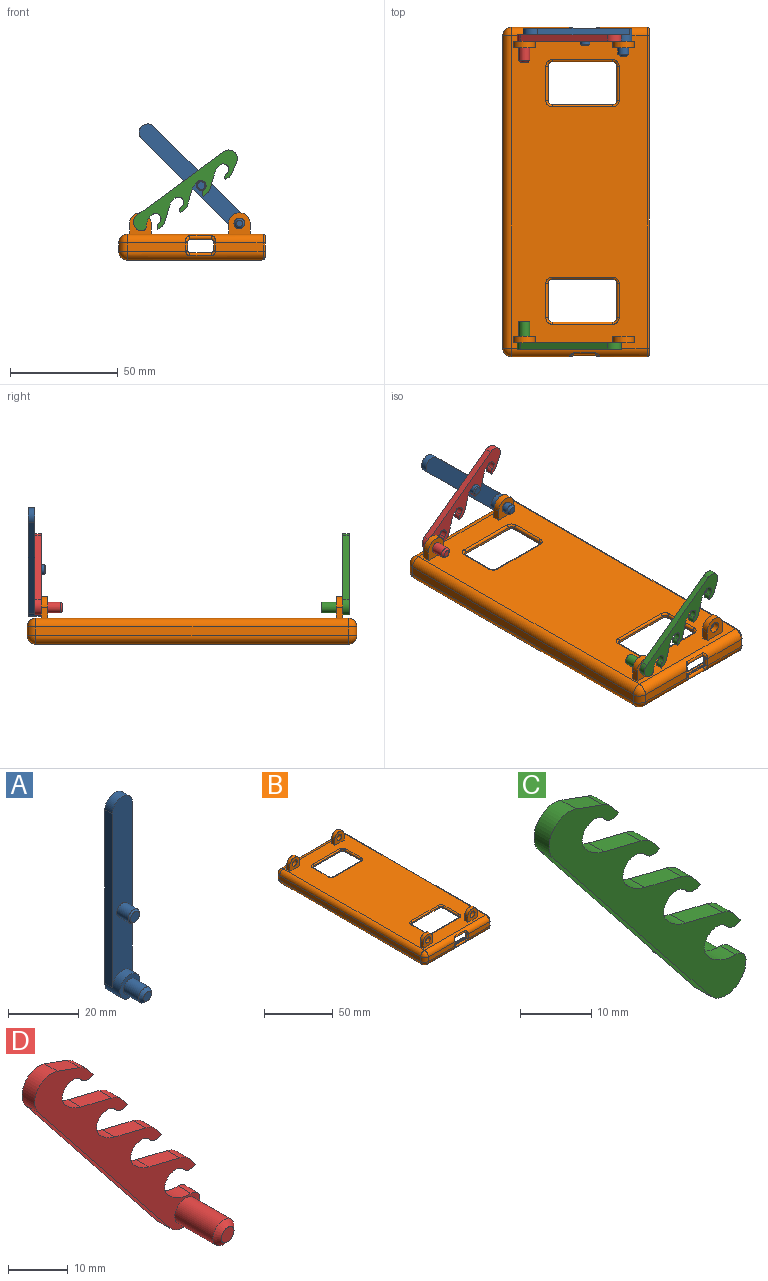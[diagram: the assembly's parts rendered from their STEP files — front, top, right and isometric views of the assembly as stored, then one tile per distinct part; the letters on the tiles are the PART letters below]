
ASSEMBLY  parts=4 mates=7
PART A: 13 faces, bbox 8x13x68 mm
  f0: plane 60x3mm, normal (-1,0,0), area 180mm2, adj f1,f3,f4,f5
  f1: cylinder r=4mm len=8mm, axis (0,1,0), area 113.1mm2, adj f0,f2,f4,f5,f6
  f2: plane 60x3mm, normal (1,0,0), area 180mm2, adj f1,f3,f4,f5
  f3: cylinder r=4mm len=8mm, axis (0,1,0), area 37.7mm2, adj f0,f2,f4,f5
  f4: plane 64x8mm, normal (0,-1,0), area 464.1mm2, adj f0,f1,f2,f3,f9
  f5: plane 68x8mm, normal (0,1,0), area 530.3mm2, adj f0,f1,f2,f3
  f6: plane 8x8mm, normal (0,-1,0), area 30.6mm2, adj f1,f8
  f7: plane 3x3mm, normal (0,-1,0), area 7.1mm2, adj f11
  f8: cylinder r=2.5mm len=6mm, axis (0,1,0), area 94.2mm2, adj f6,f11
  f9: cylinder r=2.25mm len=4.5mm, axis (0,1,0), area 63.6mm2, adj f4,f12
  f10: plane 3.5x3.5mm, normal (0,-1,0), area 9.6mm2, adj f12
  f11: cone r=1.5mm half-angle=45deg, axis (0,1,0), area 17.8mm2, adj f7,f8
  f12: cone r=1.75mm half-angle=45deg, axis (0,1,0), area 8.9mm2, adj f9,f10
PART B: 152 faces, bbox 68.1x155x22 mm
  f0: plane 145x63mm, normal (0,0,1), area 7534.5mm2, adj f9,f10,f14,f86,f104,f105,f106,f107
  f1: plane 145x63mm, normal (0,0,-1), area 7861.9mm2, adj f23,f24,f30,f66,f67,f68,f69,f70
  f2: plane 145x62.24mm, normal (0,0,-1), area 281.5mm2, adj f11,f12,f21,f95,f96,f97,f98,f99
  f3: plane 27.06x4mm, normal (0,1,0), area 108mm2, adj f9,f12,f17,f74,f75
  f4: plane 27.06x4mm, normal (0,-1,0), area 108mm2, adj f10,f11,f18,f60,f62
  f5: plane 22.06x4mm, normal (0,-1,0), area 88mm2, adj f10,f11,f59,f61,f90
  f6: plane 28.13x4mm, normal (0,-1,0), area 112mm2, adj f23,f28,f33,f42,f44
  f7: plane 28.13x4mm, normal (0,1,0), area 112mm2, adj f24,f26,f34,f49,f52
  f8: plane 22.06x4mm, normal (0,1,0), area 88mm2, adj f9,f12,f83,f85,f89
  f9: cylinder r=4mm len=63mm, axis (1,0,0), area 344mm2, adj f0,f3,f8,f15,f76,f78,f80,f82
  f10: cylinder r=4mm len=63mm, axis (1,0,0), area 344mm2, adj f0,f4,f5,f16,f54,f55,f56,f57
  f11: cylinder r=4mm len=63mm, axis (1,0,0), area 368.3mm2, adj f2,f4,f5,f20,f63,f64,f65,f92
  f12: cylinder r=4mm len=63mm, axis (1,0,0), area 368.3mm2, adj f2,f3,f8,f19,f77,f79,f81,f91
  f13: plane 145x4mm, normal (-1,0,0), area 580mm2, adj f14,f17,f18,f21
  f14: cylinder r=4mm len=145mm, axis (0,1,0), area 911.1mm2, adj f0,f13,f15,f16
  f15: sphere r=4mm, area 25.1mm2, adj f9,f14,f17
  f16: sphere r=4mm, area 25.1mm2, adj f10,f14,f18
  f17: cylinder r=4mm len=4mm, axis (0,0,-1), area 25.1mm2, adj f3,f13,f15,f19
  f18: cylinder r=4mm len=4mm, axis (0,0,1), area 25.1mm2, adj f4,f13,f16,f20
  f19: sphere r=4mm, area 25.1mm2, adj f12,f17,f21
  f20: sphere r=4mm, area 25.1mm2, adj f11,f18,f21
  f21: cylinder r=4mm len=145mm, axis (0,-1,0), area 911.1mm2, adj f2,f13,f19,f20
  f22: plane 23.13x4mm, normal (0,-1,0), area 92mm2, adj f23,f28,f40,f43,f89
  f23: cylinder r=2mm len=63mm, axis (1,0,0), area 178.1mm2, adj f1,f6,f22,f31,f38,f39,f43,f44
  f24: cylinder r=2mm len=63mm, axis (1,0,0), area 178.1mm2, adj f1,f7,f25,f32,f46,f47,f48,f49
  f25: plane 23.13x4mm, normal (0,1,0), area 92mm2, adj f24,f26,f50,f53,f90
  f26: cylinder r=2mm len=63mm, axis (1,0,0), area 191.9mm2, adj f7,f25,f27,f36,f51,f52,f53,f92
  f27: plane 145x62.24mm, normal (0,0,1), area 281.5mm2, adj f26,f28,f37,f95,f96,f97,f98,f99
  f28: cylinder r=2mm len=63mm, axis (1,0,0), area 191.9mm2, adj f6,f22,f27,f35,f40,f41,f42,f91
  f29: plane 145x4mm, normal (1,0,0), area 580mm2, adj f30,f33,f34,f37
  f30: cylinder r=2mm len=145mm, axis (0,1,0), area 455.5mm2, adj f1,f29,f31,f32
  f31: sphere r=2mm, area 6.3mm2, adj f23,f30,f33
  f32: sphere r=2mm, area 6.3mm2, adj f24,f30,f34
  f33: cylinder r=2mm len=4mm, axis (0,0,-1), area 12.6mm2, adj f6,f29,f31,f35
  f34: cylinder r=2mm len=4mm, axis (0,0,1), area 12.6mm2, adj f7,f29,f32,f36
  f35: sphere r=2mm, area 6.3mm2, adj f28,f33,f37
  f36: sphere r=2mm, area 6.3mm2, adj f26,f34,f37
  f37: cylinder r=2mm len=145mm, axis (0,-1,0), area 455.5mm2, adj f27,f29,f35,f36
  f38: plane 10x0.34mm, normal (0,0,-1), area 3.4mm2, adj f23,f39,f45,f80
  f39: cylinder r=1mm len=1.64mm, axis (0,-1,0), area 1.1mm2, adj f23,f38,f43,f82
  f40: cylinder r=1mm len=1.06mm, axis (0,-1,0), area 1.3mm2, adj f22,f28,f41,f43,f81,f83
  f41: plane 10x0.66mm, normal (0,0,1), area 6.6mm2, adj f28,f40,f42,f79
  f42: cylinder r=1mm len=1.06mm, axis (0,-1,0), area 1.3mm2, adj f6,f28,f41,f44,f75,f77
  f43: plane 4x1.06mm, normal (-1,0,0), area 4mm2, adj f22,f23,f39,f40,f84,f85
  f44: plane 4x1.06mm, normal (1,0,0), area 4mm2, adj f6,f23,f42,f45,f74,f76
  f45: cylinder r=1mm len=1.64mm, axis (0,-1,0), area 1.1mm2, adj f23,f38,f44,f78
  f46: cylinder r=1mm len=1.64mm, axis (0,-1,0), area 1.1mm2, adj f24,f48,f49,f56
  f47: cylinder r=1mm len=1.64mm, axis (0,-1,0), area 1.1mm2, adj f24,f48,f50,f55
  f48: plane 10x0.34mm, normal (0,0,-1), area 3.4mm2, adj f24,f46,f47,f54
  f49: plane 4x1.06mm, normal (1,0,0), area 4mm2, adj f7,f24,f46,f52,f58,f60
  f50: plane 4x1.06mm, normal (-1,0,0), area 4mm2, adj f24,f25,f47,f53,f57,f59
  f51: plane 10x0.66mm, normal (0,0,1), area 6.6mm2, adj f26,f52,f53,f65
  f52: cylinder r=1mm len=1.06mm, axis (0,-1,0), area 1.3mm2, adj f7,f26,f49,f51,f62,f64
  f53: cylinder r=1mm len=1.06mm, axis (0,-1,0), area 1.3mm2, adj f25,f26,f50,f51,f61,f63
  f54: cylinder r=1mm len=10mm, axis (1,0,0), area 25.6mm2, adj f10,f48,f55,f56
  f55: bspline ~3.32x3.18mm, area 5.3mm2, adj f10,f47,f54,f57
  f56: bspline ~3.32x2.88mm, area 5.3mm2, adj f10,f46,f54,f58
  f57: torus R=3mm, axis (-1,0,0), area 1mm2, adj f10,f50,f55,f59
  f58: torus R=3mm, axis (-1,0,0), area 1mm2, adj f10,f49,f56,f60
  f59: cylinder r=1mm len=3.5mm, axis (0,0,1), area 5.5mm2, adj f5,f50,f57,f61
  f60: cylinder r=1mm len=3.5mm, axis (0,0,-1), area 5.5mm2, adj f4,f49,f58,f62
  f61: torus R=2mm, axis (0,1,0), area 0.5mm2, adj f5,f53,f59,f63
  f62: torus R=2mm, axis (0,1,0), area 0.5mm2, adj f4,f52,f60,f64
  f63: bspline ~2.57x2.42mm, area 3.6mm2, adj f11,f53,f61,f65
  f64: bspline ~2.57x2.42mm, area 3.6mm2, adj f11,f52,f62,f65
  f65: cylinder r=1mm len=10mm, axis (1,0,0), area 20.9mm2, adj f11,f51,f63,f64
  f66: plane 28x1mm, normal (0,1,0), area 28mm2, adj f1,f67,f73,f104
  f67: cylinder r=2mm len=2mm, axis (0,0,1), area 3.1mm2, adj f1,f66,f68,f105
  f68: plane 16x1mm, normal (-1,0,0), area 16mm2, adj f1,f67,f69,f107
  f69: cylinder r=2mm len=2mm, axis (0,0,1), area 3.1mm2, adj f1,f68,f70,f109
  f70: plane 28x1mm, normal (0,-1,0), area 28mm2, adj f1,f69,f71,f111
  f71: cylinder r=2mm len=2mm, axis (0,0,1), area 3.1mm2, adj f1,f70,f72,f110
  f72: plane 16x1mm, normal (1,0,0), area 16mm2, adj f1,f71,f73,f108
  f73: cylinder r=2mm len=2mm, axis (0,0,1), area 3.1mm2, adj f1,f66,f72,f106
  f74: cylinder r=1mm len=3.5mm, axis (0,0,-1), area 5.5mm2, adj f3,f44,f75,f76
  f75: torus R=2mm, axis (0,1,0), area 0.5mm2, adj f3,f42,f74,f77
  f76: torus R=3mm, axis (-1,0,0), area 1mm2, adj f9,f44,f74,f78
  f77: bspline ~2.57x2.42mm, area 3.6mm2, adj f12,f42,f75,f79
  f78: bspline ~3.32x3.18mm, area 5.3mm2, adj f9,f45,f76,f80
  f79: cylinder r=1mm len=10mm, axis (1,0,0), area 20.9mm2, adj f12,f41,f77,f81
  f80: cylinder r=1mm len=10mm, axis (1,0,0), area 25.6mm2, adj f9,f38,f78,f82
  f81: bspline ~2.57x2.42mm, area 3.6mm2, adj f12,f40,f79,f83
  f82: bspline ~3.32x3.18mm, area 5.3mm2, adj f9,f39,f80,f84
  f83: torus R=2mm, axis (0,1,0), area 0.5mm2, adj f8,f40,f81,f85
  f84: torus R=3mm, axis (-1,0,0), area 1mm2, adj f9,f43,f82,f85
  f85: cylinder r=1mm len=3.5mm, axis (0,0,1), area 5.5mm2, adj f8,f43,f83,f84
  f86: cylinder r=1mm len=145mm, axis (0,1,0), area 455.5mm2, adj f0,f1,f87,f88
  f87: torus R=3mm, axis (1,0,0), area 14.8mm2, adj f9,f23,f86,f89
  f88: torus R=3mm, axis (1,0,0), area 14.8mm2, adj f10,f24,f86,f90
  f89: cylinder r=1mm len=4mm, axis (0,0,-1), area 12.6mm2, adj f8,f22,f87,f91
  f90: cylinder r=1mm len=4mm, axis (0,0,1), area 12.6mm2, adj f5,f25,f88,f92
  f91: torus R=3mm, axis (1,0,0), area 7.9mm2, adj f12,f28,f89,f93,f102
  f92: torus R=3mm, axis (1,0,0), area 7.9mm2, adj f11,f26,f90,f94,f103
  f93: bspline ~3.73x2.32mm, area 3.6mm2, adj f28,f91,f95,f102
  f94: bspline ~3.73x2.32mm, area 3.6mm2, adj f26,f92,f96,f103
  f95: torus R=3mm, axis (0,0,1), area 9.6mm2, adj f2,f27,f93,f97,f102
  f96: torus R=3mm, axis (0,0,1), area 9.6mm2, adj f2,f27,f94,f98,f103
  f97: cylinder r=1mm len=53mm, axis (1,0,0), area 166.5mm2, adj f2,f27,f95,f99
  f98: cylinder r=1mm len=53mm, axis (-1,0,0), area 166.5mm2, adj f2,f27,f96,f100
  f99: torus R=6mm, axis (0,0,1), area 26.5mm2, adj f2,f27,f97,f101
  f100: torus R=6mm, axis (0,0,1), area 26.5mm2, adj f2,f27,f98,f101
  f101: cylinder r=1mm len=131mm, axis (0,1,0), area 411.5mm2, adj f2,f27,f99,f100
  f102: bspline ~4.62x2.29mm, area 5.4mm2, adj f12,f91,f93,f95
  f103: bspline ~4.62x2.29mm, area 5.4mm2, adj f11,f92,f94,f96
  f104: cylinder r=1mm len=28mm, axis (-1,0,0), area 44mm2, adj f0,f66,f105,f106
  f105: torus R=3mm, axis (0,0,1), area 5.8mm2, adj f0,f67,f104,f107
  f106: torus R=3mm, axis (0,0,1), area 5.8mm2, adj f0,f73,f104,f108
  f107: cylinder r=1mm len=16mm, axis (0,-1,0), area 25.1mm2, adj f0,f68,f105,f109
  f108: cylinder r=1mm len=16mm, axis (0,1,0), area 25.1mm2, adj f0,f72,f106,f110
  f109: torus R=3mm, axis (0,0,1), area 5.8mm2, adj f0,f69,f107,f111
  f110: torus R=3mm, axis (0,0,1), area 5.8mm2, adj f0,f71,f108,f111
  f111: cylinder r=1mm len=28mm, axis (1,0,0), area 44mm2, adj f0,f70,f109,f110
  f112: plane 28x1mm, normal (0,-1,0), area 28mm2, adj f1,f113,f119,f120
  f113: cylinder r=2mm len=2mm, axis (0,0,1), area 3.1mm2, adj f1,f112,f114,f122
  f114: plane 16x1mm, normal (1,0,0), area 16mm2, adj f1,f113,f115,f124
  f115: cylinder r=2mm len=2mm, axis (0,0,1), area 3.1mm2, adj f1,f114,f116,f126
  f116: plane 28x1mm, normal (0,1,0), area 28mm2, adj f1,f115,f117,f127
  f117: cylinder r=2mm len=2mm, axis (0,0,1), area 3.1mm2, adj f1,f116,f118,f125
  f118: plane 16x1mm, normal (-1,0,0), area 16mm2, adj f1,f117,f119,f123
  f119: cylinder r=2mm len=2mm, axis (0,0,1), area 3.1mm2, adj f1,f112,f118,f121
  f120: cylinder r=1mm len=28mm, axis (1,0,0), area 44mm2, adj f0,f112,f121,f122
  f121: torus R=3mm, axis (0,0,1), area 5.8mm2, adj f0,f119,f120,f123
  f122: torus R=3mm, axis (0,0,1), area 5.8mm2, adj f0,f113,f120,f124
  f123: cylinder r=1mm len=16mm, axis (0,-1,0), area 25.1mm2, adj f0,f118,f121,f125
  f124: cylinder r=1mm len=16mm, axis (0,1,0), area 25.1mm2, adj f0,f114,f122,f126
  f125: torus R=3mm, axis (0,0,1), area 5.8mm2, adj f0,f117,f123,f127
  f126: torus R=3mm, axis (0,0,1), area 5.8mm2, adj f0,f115,f124,f127
  f127: cylinder r=1mm len=28mm, axis (-1,0,0), area 44mm2, adj f0,f116,f125,f126
  f128: plane 5x3mm, normal (1,0,0), area 15mm2, adj f0,f129,f132,f133
  f129: cylinder r=5mm len=10mm, axis (0,1,0), area 47.1mm2, adj f128,f130,f132,f133
  f130: plane 5x3mm, normal (-1,0,0), area 15mm2, adj f0,f129,f132,f133
  f131: cylinder r=2.5mm len=5mm, axis (0,1,0), area 47.1mm2, adj f132,f133
  f132: plane 10x10mm, normal (0,-1,0), area 69.6mm2, adj f0,f128,f129,f130,f131
  f133: plane 10x10mm, normal (0,1,0), area 69.6mm2, adj f0,f128,f129,f130,f131
  f134: plane 5x3mm, normal (1,0,0), area 15mm2, adj f0,f137,f138,f139
  f135: plane 5x3mm, normal (-1,0,0), area 15mm2, adj f0,f137,f138,f139
  f136: cylinder r=2.5mm len=5mm, axis (0,-1,0), area 47.1mm2, adj f138,f139
  f137: cylinder r=5mm len=10mm, axis (0,-1,0), area 47.1mm2, adj f134,f135,f138,f139
  f138: plane 10x10mm, normal (0,1,0), area 69.6mm2, adj f0,f134,f135,f136,f137
  f139: plane 10x10mm, normal (0,-1,0), area 69.6mm2, adj f0,f134,f135,f136,f137
  f140: plane 5x3mm, normal (-1,0,0), area 15mm2, adj f0,f143,f144,f145
  f141: plane 5x3mm, normal (1,0,0), area 15mm2, adj f0,f143,f144,f145
  f142: cylinder r=2.5mm len=5mm, axis (0,1,0), area 47.1mm2, adj f144,f145
  f143: cylinder r=5mm len=10mm, axis (0,1,0), area 47.1mm2, adj f140,f141,f144,f145
  f144: plane 10x10mm, normal (0,-1,0), area 69.6mm2, adj f0,f140,f141,f142,f143
  f145: plane 10x10mm, normal (0,1,0), area 69.6mm2, adj f0,f140,f141,f142,f143
  f146: plane 5x3mm, normal (-1,0,0), area 15mm2, adj f0,f147,f150,f151
  f147: cylinder r=5mm len=10mm, axis (0,-1,0), area 47.1mm2, adj f146,f148,f150,f151
  f148: plane 5x3mm, normal (1,0,0), area 15mm2, adj f0,f147,f150,f151
  f149: cylinder r=2.5mm len=5mm, axis (0,-1,0), area 47.1mm2, adj f150,f151
  f150: plane 10x10mm, normal (0,1,0), area 69.6mm2, adj f0,f146,f147,f148,f149
  f151: plane 10x10mm, normal (0,-1,0), area 69.6mm2, adj f0,f146,f147,f148,f149
PART C: 32 faces, bbox 39.1x13x47.2 mm
  f0: plane 7.33x3mm, normal (0.24,0,0.97), area 22.6mm2, adj f1,f27,f28,f29
  f1: cylinder r=7mm len=3.8mm, axis (0,1,0), area 13.8mm2, adj f0,f2,f28,f29
  f2: cylinder r=2.5mm len=4.46mm, axis (0,1,0), area 23.6mm2, adj f1,f3,f28,f29
  f3: cylinder r=2mm len=3mm, axis (0,1,0), area 9.4mm2, adj f2,f4,f28,f29
  f4: plane 3x1.57mm, normal (0.78,0,0.62), area 6mm2, adj f3,f5,f28,f29
  f5: cylinder r=4.5mm len=3mm, axis (0,1,0), area 7.5mm2, adj f4,f6,f28,f29
  f6: plane 5.24x3mm, normal (0.34,0,0.94), area 16.7mm2, adj f5,f7,f28,f29
  f7: cylinder r=4mm len=6.49mm, axis (0,1,0), area 31.1mm2, adj f6,f8,f28,f29
  f8: plane 39.16x31.09mm, normal (-0.78,0,-0.62), area 150mm2, adj f7,f9,f28,f29
  f9: cylinder r=4mm len=7.13mm, axis (0,1,0), area 30mm2, adj f8,f10,f28,f29
  f10: cylinder r=2mm len=3mm, axis (0,1,0), area 9.4mm2, adj f9,f11,f28,f29
  f11: cylinder r=7mm len=5.68mm, axis (0,1,0), area 19.5mm2, adj f10,f12,f28,f29
  f12: cylinder r=2.5mm len=4.46mm, axis (0,1,0), area 23.6mm2, adj f11,f13,f28,f29
  f13: cylinder r=2mm len=3mm, axis (0,1,0), area 9.4mm2, adj f12,f14,f28,f29
  f14: plane 3x1.57mm, normal (0.78,0,0.62), area 6mm2, adj f13,f15,f28,f29
  f15: cylinder r=4.5mm len=3mm, axis (0,1,0), area 8.9mm2, adj f14,f16,f28,f29
  f16: plane 7.33x3mm, normal (0.24,0,0.97), area 22.6mm2, adj f15,f17,f28,f29
  f17: cylinder r=7mm len=3.8mm, axis (0,1,0), area 13.8mm2, adj f16,f18,f28,f29
  f18: cylinder r=2.5mm len=4.46mm, axis (0,1,0), area 23.6mm2, adj f17,f19,f28,f29
  f19: cylinder r=2mm len=3mm, axis (0,1,0), area 9.4mm2, adj f18,f20,f28,f29
  f20: plane 3x1.57mm, normal (0.78,0,0.62), area 6mm2, adj f19,f21,f28,f29
  f21: cylinder r=4.5mm len=3mm, axis (0,1,0), area 8.9mm2, adj f20,f22,f28,f29
  f22: plane 7.33x3mm, normal (0.24,0,0.97), area 22.6mm2, adj f21,f23,f28,f29
  f23: cylinder r=7mm len=3.8mm, axis (0,1,0), area 13.8mm2, adj f22,f24,f28,f29
  f24: cylinder r=2.5mm len=4.46mm, axis (0,1,0), area 23.6mm2, adj f23,f25,f28,f29
  f25: cylinder r=2mm len=3mm, axis (0,1,0), area 9.4mm2, adj f24,f26,f28,f29
  f26: plane 3x1.57mm, normal (0.78,0,0.62), area 6mm2, adj f25,f27,f28,f29
  f27: cylinder r=4.5mm len=3mm, axis (0,1,0), area 8.9mm2, adj f0,f26,f28,f29
  f28: plane 47.16x39.09mm, normal (0,-1,0), area 388.5mm2, adj f0,f1,f2,f3,f4,f5,f6,f7
  f29: plane 47.16x39.09mm, normal (0,1,0), area 368.9mm2, adj f0,f1,f2,f3,f4,f5,f6,f7
  f30: cylinder r=2.5mm len=10mm, axis (0,-1,0), area 157.1mm2, adj f29,f31
  f31: plane 5x5mm, normal (0,1,0), area 19.6mm2, adj f30
PART D: 33 faces, bbox 39.1x13x47.2 mm
  f0: plane 7.33x3mm, normal (0.24,0,0.97), area 22.6mm2, adj f1,f27,f28,f29
  f1: cylinder r=7mm len=3.8mm, axis (0,-1,0), area 13.8mm2, adj f0,f2,f28,f29
  f2: cylinder r=2.5mm len=4.46mm, axis (0,-1,0), area 23.6mm2, adj f1,f3,f28,f29
  f3: cylinder r=2mm len=3mm, axis (0,-1,0), area 9.4mm2, adj f2,f4,f28,f29
  f4: plane 3x1.57mm, normal (0.78,0,0.62), area 6mm2, adj f3,f5,f28,f29
  f5: cylinder r=4.5mm len=3mm, axis (0,-1,0), area 7.5mm2, adj f4,f6,f28,f29
  f6: plane 5.24x3mm, normal (0.34,0,0.94), area 16.7mm2, adj f5,f7,f28,f29
  f7: cylinder r=4mm len=6.49mm, axis (0,-1,0), area 31.1mm2, adj f6,f8,f28,f29
  f8: plane 39.16x31.09mm, normal (-0.78,0,-0.62), area 150mm2, adj f7,f9,f28,f29
  f9: cylinder r=4mm len=7.13mm, axis (0,-1,0), area 30mm2, adj f8,f10,f28,f29
  f10: cylinder r=2mm len=3mm, axis (0,-1,0), area 9.4mm2, adj f9,f11,f28,f29
  f11: cylinder r=7mm len=5.68mm, axis (0,-1,0), area 19.5mm2, adj f10,f12,f28,f29
  f12: cylinder r=2.5mm len=4.46mm, axis (0,-1,0), area 23.6mm2, adj f11,f13,f28,f29
  f13: cylinder r=2mm len=3mm, axis (0,-1,0), area 9.4mm2, adj f12,f14,f28,f29
  f14: plane 3x1.57mm, normal (0.78,0,0.62), area 6mm2, adj f13,f15,f28,f29
  f15: cylinder r=4.5mm len=3mm, axis (0,-1,0), area 8.9mm2, adj f14,f16,f28,f29
  f16: plane 7.33x3mm, normal (0.24,0,0.97), area 22.6mm2, adj f15,f17,f28,f29
  f17: cylinder r=7mm len=3.8mm, axis (0,-1,0), area 13.8mm2, adj f16,f18,f28,f29
  f18: cylinder r=2.5mm len=4.46mm, axis (0,-1,0), area 23.6mm2, adj f17,f19,f28,f29
  f19: cylinder r=2mm len=3mm, axis (0,-1,0), area 9.4mm2, adj f18,f20,f28,f29
  f20: plane 3x1.57mm, normal (0.78,0,0.62), area 6mm2, adj f19,f21,f28,f29
  f21: cylinder r=4.5mm len=3mm, axis (0,-1,0), area 8.9mm2, adj f20,f22,f28,f29
  f22: plane 7.33x3mm, normal (0.24,0,0.97), area 22.6mm2, adj f21,f23,f28,f29
  f23: cylinder r=7mm len=3.8mm, axis (0,-1,0), area 13.8mm2, adj f22,f24,f28,f29
  f24: cylinder r=2.5mm len=4.46mm, axis (0,-1,0), area 23.6mm2, adj f23,f25,f28,f29
  f25: cylinder r=2mm len=3mm, axis (0,-1,0), area 9.4mm2, adj f24,f26,f28,f29
  f26: plane 3x1.57mm, normal (0.78,0,0.62), area 6mm2, adj f25,f27,f28,f29
  f27: cylinder r=4.5mm len=3mm, axis (0,-1,0), area 8.9mm2, adj f0,f26,f28,f29
  f28: plane 47.16x39.09mm, normal (0,1,0), area 388.5mm2, adj f0,f1,f2,f3,f4,f5,f6,f7
  f29: plane 47.16x39.09mm, normal (0,-1,0), area 368.9mm2, adj f0,f1,f2,f3,f4,f5,f6,f7
  f30: cylinder r=2.5mm len=9mm, axis (0,1,0), area 141.4mm2, adj f29,f32
  f31: plane 3x3mm, normal (0,-1,0), area 7.1mm2, adj f32
  f32: cone r=1.5mm half-angle=45deg, axis (0,1,0), area 17.8mm2, adj f30,f31
PLACE A rot(axis=(0,-1,0),45.2deg) t=(45.05,6,-10.15)mm
PLACE B at identity fixed
PLACE C rot(axis=(0,1,0),92.2deg) t=(-95.96,0,-65.44)mm
PLACE D rot(axis=(0,1,0),92.2deg) t=(-95.96,0,-65.44)mm
MATE planar C.f9 <-> B.f129  axis (0,1,0) through (-62.2,-70,11.58)mm
MATE cylindrical D.f30 <-> B.f129  axis (0,1,0) through (-63,70,11)mm
MATE cylindrical A.f1 <-> B.f142  axis (0,1,0) through (-17,70,11)mm
MATE cylindrical C.f30 <-> B.f129  axis (0,-1,0) through (-63,-70,11)mm
MATE planar D.f8 <-> C.f8  axis (-0.59,0,0.81) through (-44.4,71.5,29.59)mm
MATE planar D.f9 <-> B.f129  axis (0,-1,0) through (-62.2,70,11.58)mm
MATE planar A.f1 <-> B.f142  axis (0,-1,0) through (-17,70,11)mm
